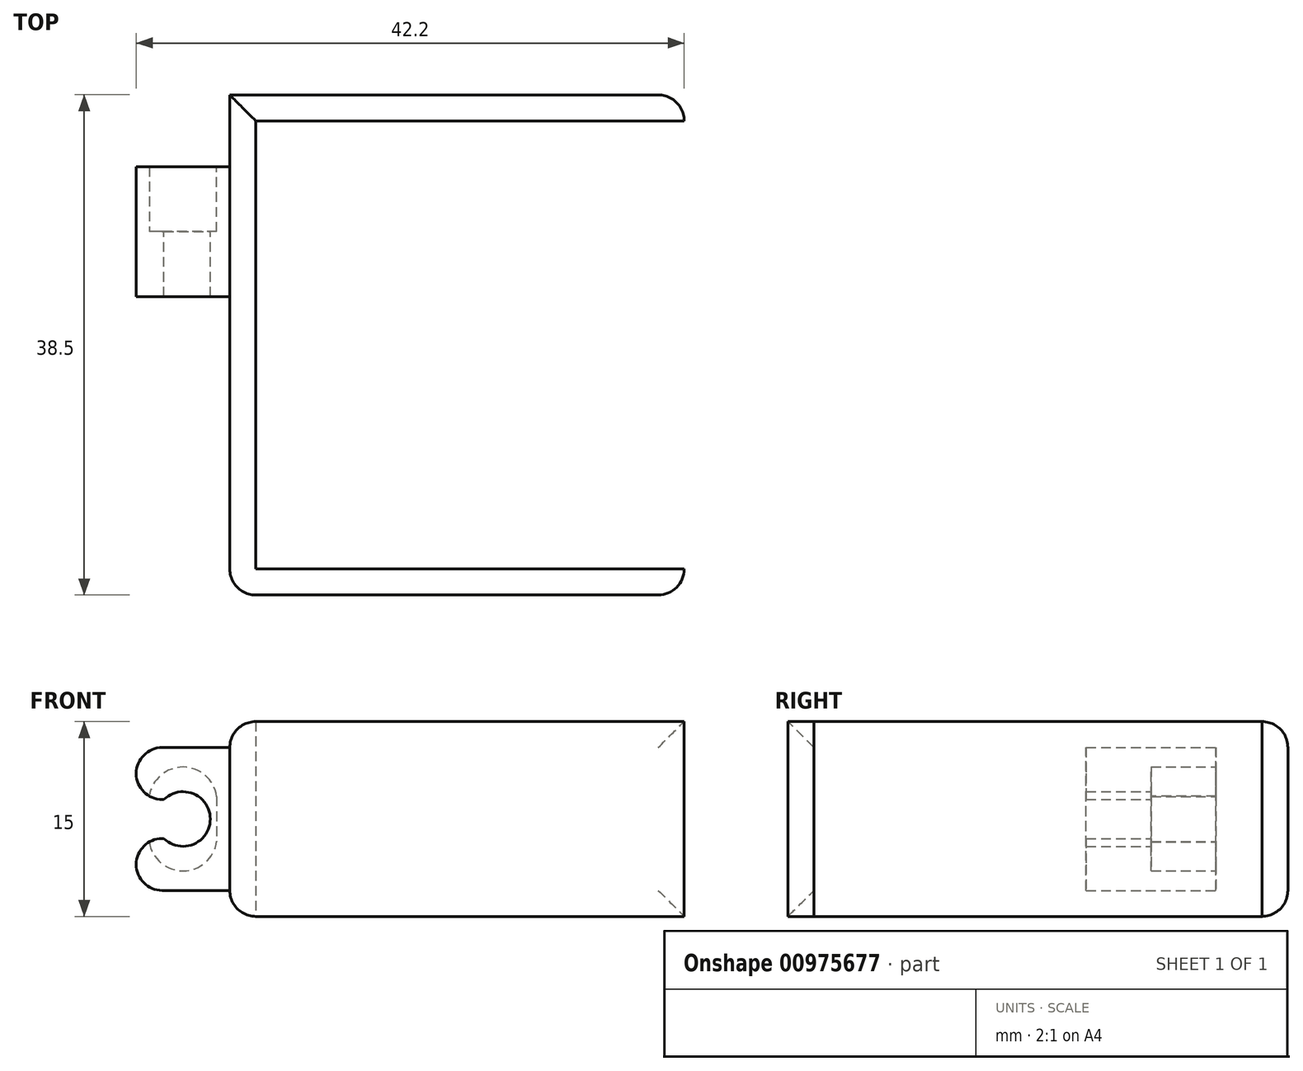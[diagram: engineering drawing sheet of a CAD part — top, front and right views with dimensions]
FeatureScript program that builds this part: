
annotation { "Feature Type Name" : "Feature", "Feature Type Description" : "" }
export const myFeature = defineFeature(function(context is Context, id is Id, definition is map)
    precondition{}
    {
        {
            var Q0;
            Q0=qCreatedBy(makeId("Top.planeOp"),FACE);
            var sketch = newSketch(context, id + "F0", { "sketchPlane" : qUnion([Q0])});
            skLineSegment(sketch, "E0", {"start": v(29.47, 10.54) * mm, "end": v(29.47, 8.54) * mm});
            skLineSegment(sketch, "E1", {"start": v(29.47, 8.54) * mm, "end": v(-3.53, 8.54) * mm});
            skLineSegment(sketch, "E2", {"start": v(-3.53, 8.54) * mm, "end": v(-3.53, -25.96) * mm});
            skLineSegment(sketch, "E3", {"start": v(-3.53, -25.96) * mm, "end": v(29.47, -25.96) * mm});
            skLineSegment(sketch, "E4", {"start": v(29.47, -25.96) * mm, "end": v(29.47, -27.96) * mm});
            skLineSegment(sketch, "E5", {"start": v(29.47, -27.96) * mm, "end": v(-5.53, -27.96) * mm});
            skLineSegment(sketch, "E6", {"start": v(-5.53, -27.96) * mm, "end": v(-5.53, 10.54) * mm});
            skLineSegment(sketch, "E7", {"start": v(-5.53, 10.54) * mm, "end": v(29.47, 10.54) * mm});
            skLineSegment(sketch, "E8.bottom", {"start": v(29.47, -25.96) * mm, "end": v(27.47, -25.96) * mm});
            skLineSegment(sketch, "E9.bottom", {"start": v(29.47, 8.54) * mm, "end": v(27.47, 8.54) * mm});
            skPoint(sketch, "E10", {"position": v(-5.53, -8.71) * mm});
            skSolve(sketch);
        }
        {
            var Q0;
            Q0=qSketchRegion(id+"F0",true);
            extrude(context, id + "F1", {"entities" : qUnion([Q0]), "endBound" : BoundingType.SYMMETRIC, "depth" : 15 * mm, "offsetDistance" : 25 * mm});
        }
        {
            var Q0;
            Q0=makeQuery(id+"F1.opExtrude","CAP_EDGE",EDGE,{"disambiguationData":[OSD([sQuery(id+"F0.wireOp",EDGE,"E7")])],"isStart":false});
            var Q1;
            Q1=makeQuery(id+"F1.opExtrude","CAP_EDGE",EDGE,{"disambiguationData":[OSD([sQuery(id+"F0.wireOp",EDGE,"E7")])],"isStart":true});
            var Q2;
            Q2=makeQuery(id+"F1.opExtrude","CAP_EDGE",EDGE,{"disambiguationData":[OSD([sQuery(id+"F0.wireOp",EDGE,"E6")])],"isStart":false});
            var Q3;
            Q3=makeQuery(id+"F1.opExtrude","SWEPT_EDGE",EDGE,{"disambiguationData":[OSD([sQuery(id+"F0.wireOp",EDGE,"E4"),sQuery(id+"F0.wireOp",EDGE,"E5")])]});
            var Q4;
            Q4=makeQuery(id+"F1.opExtrude","SWEPT_EDGE",EDGE,{"disambiguationData":[OSD([sQuery(id+"F0.wireOp",EDGE,"E5"),sQuery(id+"F0.wireOp",EDGE,"E6")])]});
            var Q5;
            Q5=makeQuery(id+"F1.opExtrude","SWEPT_EDGE",EDGE,{"disambiguationData":[OSD([sQuery(id+"F0.wireOp",EDGE,"E0"),sQuery(id+"F0.wireOp",EDGE,"E7")])]});
            var Q6;
            Q6=makeQuery(id+"F1.opExtrude","CAP_EDGE",EDGE,{"disambiguationData":[OSD([sQuery(id+"F0.wireOp",EDGE,"E6")])],"isStart":true});
            fillet(context, id + "F2", {"entities" : qUnion([Q0, Q1, Q2, Q3, Q4, Q5, Q6]), "radius" : 2 * mm, "tangentPropagation" : true, "defaultsChanged" : false, "vertexSettings" : [], "allowEdgeOverflow" : false});
        }
        {
            var Q0;
            Q0=qCreatedBy(makeId("Front.planeOp"),FACE);
            var sketch = newSketch(context, id + "F3", { "sketchPlane" : qUnion([Q0])});
            skArc(sketch, "E11", {"start": v(-6.53, 1.73) * mm, "mid": v(-9.13, 4) * mm, "end": v(-11.73, 1.73) * mm});
            skArc(sketch, "E12.MirrorCS", {"start": v(-6.53, -1.73) * mm, "mid": v(-9.13, -4) * mm, "end": v(-11.73, -1.73) * mm});
            skLineSegment(sketch, "E13", {"start": v(-6.53, 1.73) * mm, "end": v(-6.53, -1.73) * mm});
            skLineSegment(sketch, "E14", {"start": v(-11.73, -1.73) * mm, "end": v(-11.73, 1.73) * mm});
            skLineSegment(sketch, "E15.bottom", {"start": v(-5.53, -5.5) * mm, "end": v(-12.73, -5.5) * mm});
            skLineSegment(sketch, "E15.top", {"start": v(-5.53, 5.5) * mm, "end": v(-12.73, 5.5) * mm});
            skLineSegment(sketch, "E15.left", {"start": v(-5.53, -5.5) * mm, "end": v(-5.53, 5.5) * mm});
            skLineSegment(sketch, "E15.right", {"start": v(-12.73, -5.5) * mm, "end": v(-12.73, 5.5) * mm});
            skPoint(sketch, "E16", {"position": v(-5.53, 0) * mm});
            skPoint(sketch, "E17", {"position": v(-11.73, 0) * mm});
            skLineSegment(sketch, "E18", {"start": v(37.64, 0) * mm, "end": v(-29.42, 0) * mm, "construction": true});
            skPoint(sketch, "E18.startSnap0", {"position": v(-12.73, 0) * mm});
            skLineSegment(sketch, "E19", {"start": v(-9.13, -7) * mm, "end": v(-9.13, -7.09) * mm, "construction": true});
            skPoint(sketch, "E19.startSnap0", {"position": v(-9.13, 5.5) * mm});
            skPoint(sketch, "E19.endSnap0", {"position": v(-9.13, -5.5) * mm});
            skPoint(sketch, "E20", {"position": v(-9.13, 0) * mm});
            skCircle(sketch, "E21", {"center": v(-9.13, 0) * mm, "radius": 2.1 * mm});
            skLineSegment(sketch, "E22", {"start": v(-9.13, 7.94) * mm, "end": v(-9.13, -6.57) * mm, "construction": true});
            skLineSegment(sketch, "E23", {"start": v(-16.33, 1.5) * mm, "end": v(-5.53, 1.5) * mm, "construction": true});
            skLineSegment(sketch, "E24.MirrorCS", {"start": v(-16.33, -1.5) * mm, "end": v(-5.53, -1.5) * mm, "construction": true});
            skLineSegment(sketch, "E25", {"start": v(-12.73, 1.5) * mm, "end": v(-10.6, 1.5) * mm});
            skLineSegment(sketch, "E26", {"start": v(-12.73, -1.5) * mm, "end": v(-10.6, -1.5) * mm});
            skSolve(sketch);
        }
        {
            var Q0;
            {var subQ1=sQuery(id+"F3.wireOp",EDGE,"E13");Q0=makeQuery(id+"F3.imprint","IMPRINT",FACE,{"disambiguationData":[TD([[makeQuery(id+"F3.imprint","IMPRINT",EDGE,{"derivedFrom":subQ1}),1.0]])]});}
            extrude(context, id + "F4", {"entities" : qUnion([Q0]), "operationType" : NewBodyOperationType.ADD, "endBound" : BoundingType.SYMMETRIC, "depth" : 10 * mm, "offsetDistance" : 25 * mm});
        }
        {
            var Q0;
            {var subQ5=sQuery(id+"F3.wireOp",EDGE,"E13");Q0=makeQuery(id+"F3.imprint","IMPRINT",FACE,{"disambiguationData":[TD([[makeQuery(id+"F3.imprint","IMPRINT",EDGE,{"derivedFrom":subQ5}),-1.0]])]});}
            extrude(context, id + "F5", {"entities" : qUnion([Q0]), "operationType" : NewBodyOperationType.ADD, "depth" : 5 * mm, "offsetDistance" : 25 * mm});
        }
        {
            var Q0;
            Q0=makeQuery(id+"F4.opExtrude","SWEPT_EDGE",EDGE,{"disambiguationData":[OSD([sQuery(id+"F3.wireOp",EDGE,"E15.top"),sQuery(id+"F3.wireOp",EDGE,"E15.right")])]});
            var Q1;
            Q1=makeQuery(id+"F4.opExtrude","SWEPT_EDGE",EDGE,{"disambiguationData":[OSD([sQuery(id+"F3.wireOp",EDGE,"E15.bottom"),sQuery(id+"F3.wireOp",EDGE,"E15.right")])]});
            var Q2;
            Q2=makeQuery(id+"F4.opExtrude","SWEPT_EDGE",EDGE,{"disambiguationData":[OSD([sQuery(id+"F3.wireOp",EDGE,"E15.right"),sQuery(id+"F3.wireOp",EDGE,"E25")])]});
            var Q3;
            Q3=makeQuery(id+"F4.opExtrude","SWEPT_EDGE",EDGE,{"disambiguationData":[OSD([sQuery(id+"F3.wireOp",EDGE,"E15.right"),sQuery(id+"F3.wireOp",EDGE,"E26")])]});
            fillet(context, id + "F6", {"entities" : qUnion([Q0, Q1, Q2, Q3]), "tangentPropagation" : true, "radius" : 2 * mm, "defaultsChanged" : false, "vertexSettings" : [], "allowEdgeOverflow" : false});
        }
    });
